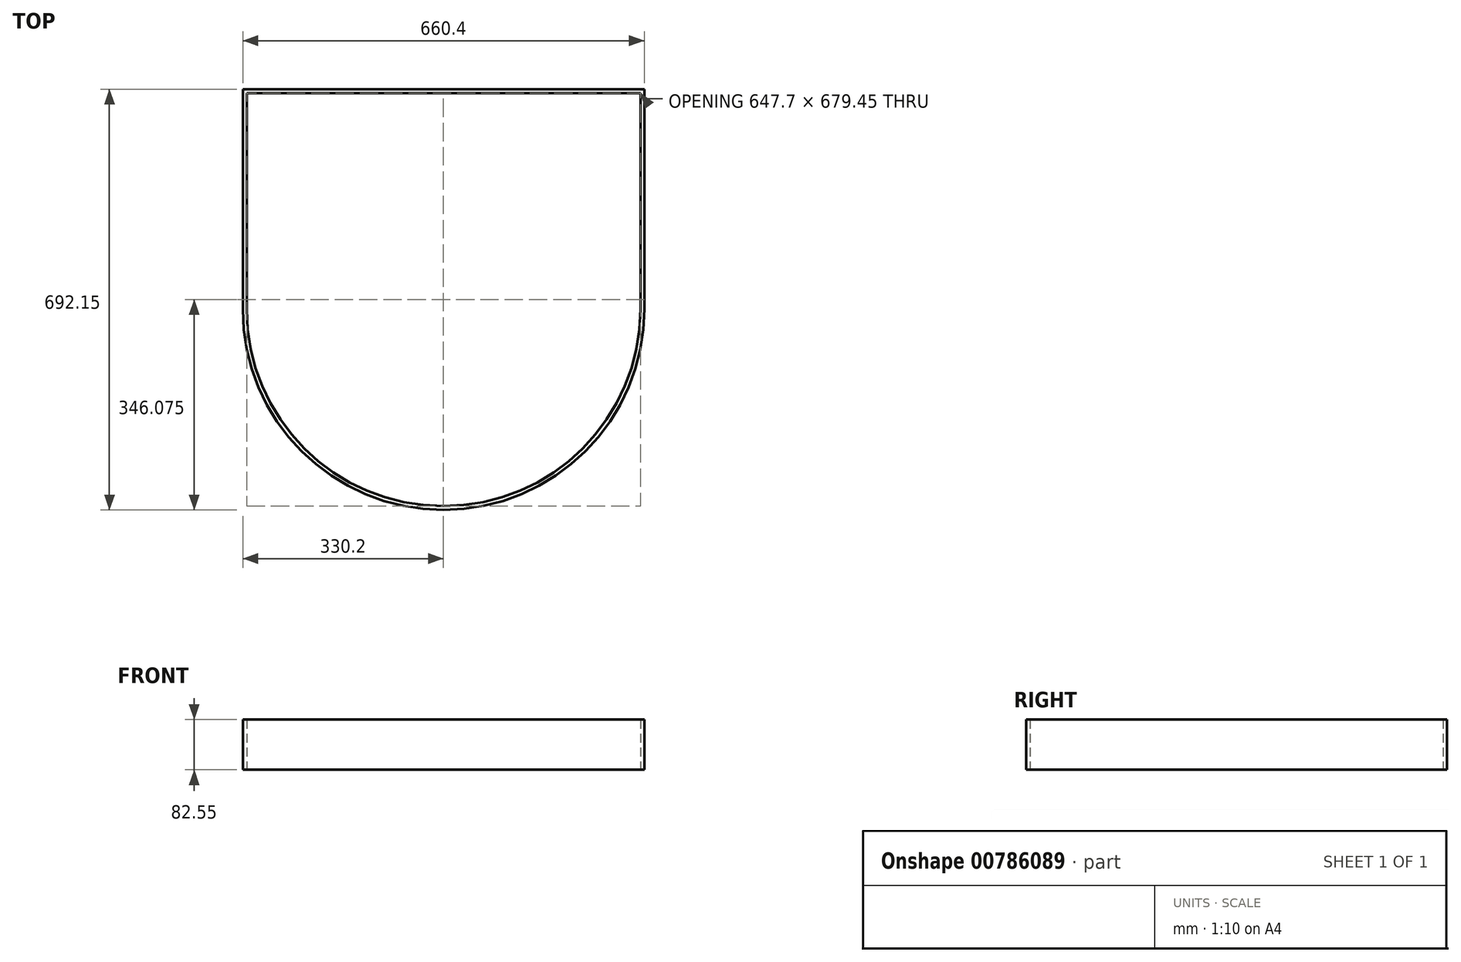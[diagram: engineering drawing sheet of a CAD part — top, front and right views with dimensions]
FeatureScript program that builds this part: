
annotation { "Feature Type Name" : "Feature", "Feature Type Description" : "" }
export const myFeature = defineFeature(function(context is Context, id is Id, definition is map)
    precondition{}
    {
        {
            var Q0;
            Q0=qCreatedBy(makeId("Top.planeOp"),FACE);
            var sketch = newSketch(context, id + "F0", { "sketchPlane" : qUnion([Q0])});
            skArc(sketch, "E0", {"start": v(330.2, 0) * mm, "mid": v(0, -330.2) * mm, "end": v(-330.2, 0) * mm});
            skLineSegment(sketch, "E1", {"start": v(-330.2, 0) * mm, "end": v(-330.2, 361.95) * mm});
            skLineSegment(sketch, "E2", {"start": v(-330.2, 361.95) * mm, "end": v(330.2, 361.95) * mm});
            skLineSegment(sketch, "E3", {"start": v(330.2, 361.95) * mm, "end": v(330.2, 0) * mm});
            skLineSegment(sketch, "E4.0", {"start": v(-323.85, 0) * mm, "end": v(-323.85, 355.6) * mm});
            skArc(sketch, "E4.1", {"start": v(323.85, 0) * mm, "mid": v(0, -323.85) * mm, "end": v(-323.85, 0) * mm});
            skLineSegment(sketch, "E4.2", {"start": v(323.85, 355.6) * mm, "end": v(323.85, 0) * mm});
            skLineSegment(sketch, "E4.3", {"start": v(-323.85, 355.6) * mm, "end": v(323.85, 355.6) * mm});
            skSolve(sketch);
        }
        {
            var Q0;
            Q0 = qSketchRegion(id + "F0", true);
            extrude(context, id + "F1", {"entities" : qUnion([Q0]), "depth" : 82.55 * mm, "offsetDistance" : 25.4 * mm});
        }
    });
